# Revit family: HVAC_COM_Firetube-Boiler-Scotch-Marine-Steam
name_source: partatom
category: Plumbing Fixtures
units: mm (PartAtom-declared; Revit-internal decimal feet)

## family parameters
Always vertical = Yes
Classification Number = 23.75.10.11.21
Cut with Voids When Loaded = No
Enable Cutting in Views = No
Maintain Annotation Orientation = No
Part Type = Normal
Room Calculation Point = No
Round Connector Dimension = Use Radius
Shared = No
Work Plane-Based = Yes

## types (1)
- as Specified
    Accent Material = ARCAT - Metal - Black
    Capacity (Gal) = 436 CF
    Clearance_Door Swing = 2' - 7"
    Clearance_Front Tube Removal = 6' - 11"
    Clearance_Rear Tube Removal = 6' - 4"
    Default Elevation = 4' - 0"
    Diameter_Blowdown Connection = 0' - 1 1/4"
    Diameter_Feedwater Inlet = 0' - 1 1/4"
    Diameter_Furnace Tube = 2' - 0"
    Diameter_Shell = 4' - 10"
    Diameter_Stack Outlet OD = 1' - 4"
    Expected Lifespan (Years) = 0
    Gross Output = 2343 MBTU/HR
    Height_Floor to Shell = 1' - 2"
    Height_Furnace CL from Floor = 2' - 5 9/16"
    Height_Steam Outlet = 6' - 0"
    Length_Blowdown 1 = 1' - 11"
    Length_Blowdown 2 = 3' - 4"
    Length_Boiler Shell = 9' - 7"
    Length_Skid = 9' - 9"
    Length_Skid from Front = 2' - 2 1/4"
    Length_Stack Outlet from Front = 8' - 3 3/4"
    Length_Steam Outlet from Front = 4' - 2"
    Maintenance Schedule (Months) = 0
    Material = ARCAT - Metal - Blue
    Second Blowdown Piping = No
    Skid Width = 6' - 0"
    Steam Output = 2415 lbs/hr at 212 degrees F
    Unit Height = 6' - 2 5/8"
    Unit Length = 12' - 6"
    Unit Width = 5' - 2"
    Warranty Duration (Years) = 0
    Width_Skid = 3' - 8"
    Width_Unit Width with Trim = 5' - 7"
    blowdownradius = 0' - 0 5/8"
    doorpanelradius = 2' - 3 1/2"
    feedwaterradius = 0' - 0 5/8"
    stackoutletradius = 0' - 8"

## geometry (parser evidence)
native form markers: Sweep x1
no freeform markers — native parametric forms only
